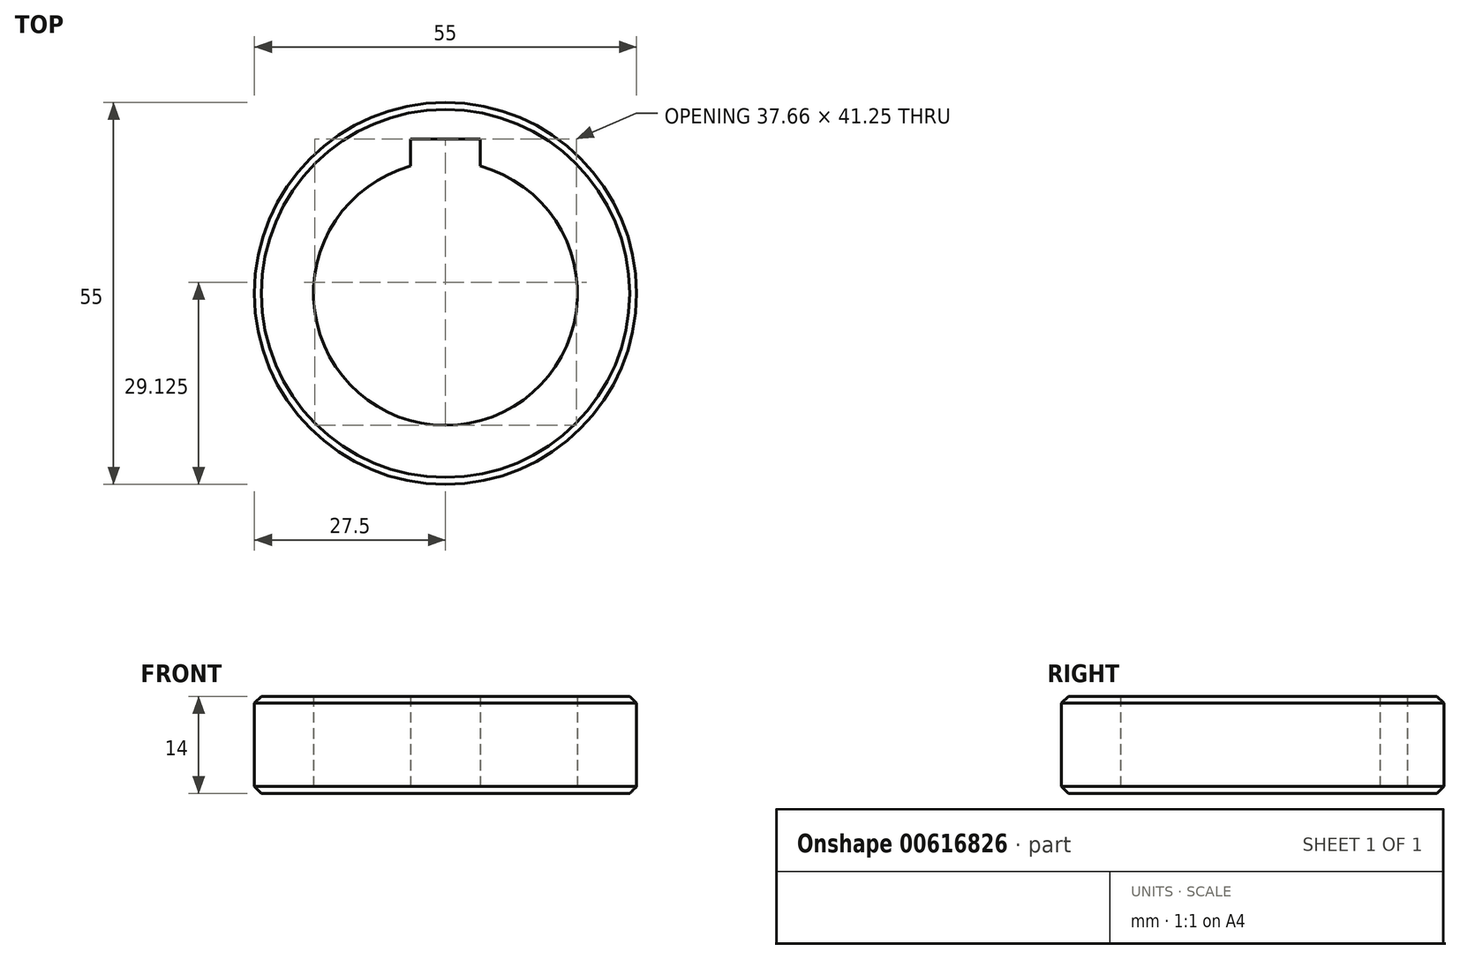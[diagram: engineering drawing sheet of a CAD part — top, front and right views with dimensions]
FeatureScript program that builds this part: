
annotation { "Feature Type Name" : "Feature", "Feature Type Description" : "" }
export const myFeature = defineFeature(function(context is Context, id is Id, definition is map)
    precondition{}
    {
        {
            var Q0;
            Q0=qCreatedBy(makeId("Top.planeOp"),FACE);
            var sketch = newSketch(context, id + "F0", { "sketchPlane" : qUnion([Q0])});
            skCircle(sketch, "E0", {"center": v(0, 0) * mm, "radius": 27.5 * mm});
            skArc(sketch, "E1", {"start": v(-5, 18.33) * mm, "mid": v(0, -19) * mm, "end": v(5, 18.33) * mm});
            skLineSegment(sketch, "E2", {"start": v(-5, 18.33) * mm, "end": v(-5, 22.25) * mm});
            skLineSegment(sketch, "E3", {"start": v(-5, 22.25) * mm, "end": v(0, 22.25) * mm});
            skLineSegment(sketch, "E4.MirrorCS", {"start": v(5, 18.33) * mm, "end": v(5, 22.25) * mm});
            skLineSegment(sketch, "E5.MirrorCS", {"start": v(5, 22.25) * mm, "end": v(0, 22.25) * mm});
            skSolve(sketch);
        }
        {
            var Q0;
            Q0 = qSketchRegion(id + "F0", true);
            extrude(context, id + "F1", {"entities" : qUnion([Q0]), "depth" : 14 * mm, "offsetDistance" : 25 * mm});
        }
        {
            var Q0;
            Q0=makeQuery(id+"F1.opExtrude","CAP_EDGE",EDGE,{"disambiguationData":[OSD([sQuery(id+"F0.wireOp",EDGE,"E0")])],"isStart":false});
            var Q1;
            Q1=makeQuery(id+"F1.opExtrude","CAP_EDGE",EDGE,{"disambiguationData":[OSD([sQuery(id+"F0.wireOp",EDGE,"E0")])],"isStart":true});
            chamfer(context, id + "F2", {"entities" : qUnion([Q0, Q1]), "width" : 1 * mm, "tangentPropagation" : true});
        }
    });
